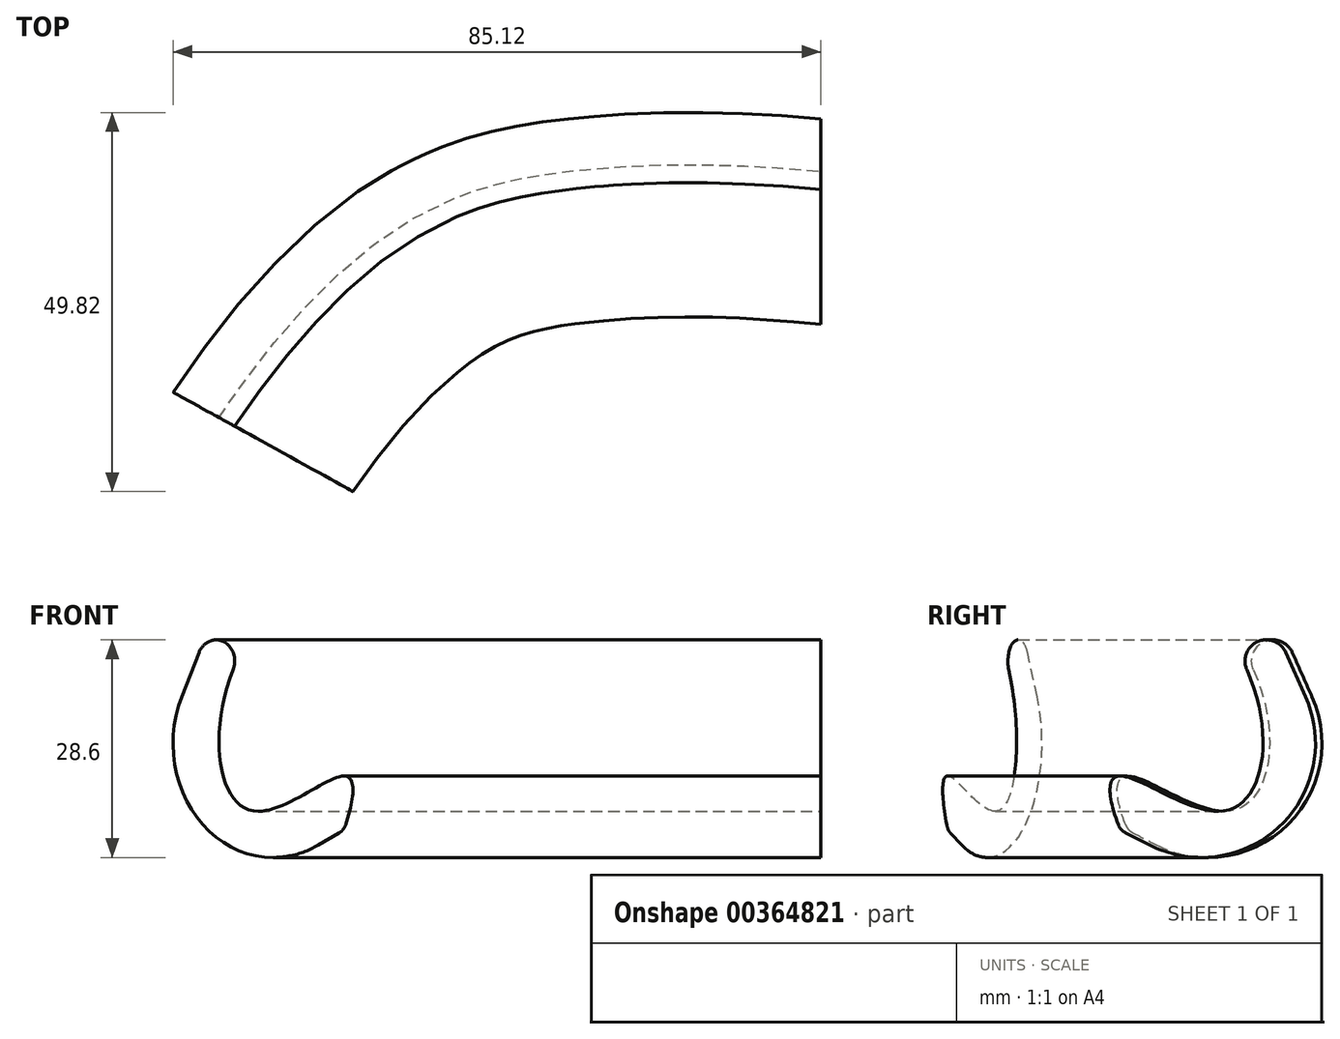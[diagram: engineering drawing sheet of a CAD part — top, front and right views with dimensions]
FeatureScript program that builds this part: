
annotation { "Feature Type Name" : "Feature", "Feature Type Description" : "" }
export const myFeature = defineFeature(function(context is Context, id is Id, definition is map)
    precondition{}
    {
        {
            var Q0;
            Q0=qCreatedBy(makeId("Right.planeOp"),FACE);
            var sketch = newSketch(context, id + "F0", { "sketchPlane" : qUnion([Q0])});
            skFitSpline(sketch, "E0", {"points": [v(-5.11, 3.54) * mm, v(-8.02, -14.99) * mm, v(-22, -10.43) * mm, v(-21.7, -17.57) * mm], "startDerivative": vector(29.4, -65.83) * mm, "endDerivative": vector(19.16, -45.51) * mm});
            skLineSegment(sketch, "E1", {"start": v(-21.02, -17.9) * mm, "end": v(-17.88, -19.5) * mm});
            skLineSegment(sketch, "E2", {"start": v(2.6, 0) * mm, "end": v(0, 5.82) * mm});
            skArc(sketch, "E3", {"start": v(0, 5.82) * mm, "mid": v(-3.7, 7.24) * mm, "end": v(-5.11, 3.54) * mm});
            skPoint(sketch, "E4.visualSharp", {"position": v(19.84, -38.61) * mm});
            skArc(sketch, "E4.filletArc", {"start": v(-17.88, -19.5) * mm, "mid": v(-0.75, -16.99) * mm, "end": v(2.6, 0) * mm});
            skArc(sketch, "E5.filletArc", {"start": v(-21.98, -16.85) * mm, "mid": v(-21.6, -17.47) * mm, "end": v(-21.02, -17.9) * mm});
            skLineSegment(sketch, "E6", {"start": v(-5.11, 3.54) * mm, "end": v(0, 5.82) * mm, "construction": true});
            skSolve(sketch);
        }
        {
            var Q0;
            Q0=qCreatedBy(makeId("Top.planeOp"),FACE);
            var sketch = newSketch(context, id + "F1", { "sketchPlane" : qUnion([Q0])});
            skFitSpline(sketch, "E7", {"points": [v(0, 0) * mm, v(-32.98, 0) * mm, v(-81.7, -33.92) * mm], "startDerivative": vector(-86.34, 7.65) * mm, "endDerivative": vector(-100.27, -148.95) * mm});
            skSolve(sketch);
        }
        {
            var Q0;
            Q0=makeQuery(id+"F0.imprint","IMPRINT",FACE,{"disambiguationData":[TD([[makeQuery(id+"F0.imprint","IMPRINT",EDGE,{"derivedFrom":sQuery(id+"F0.wireOp",EDGE,"E0")}),1.0]])]});
            var Q1;
            Q1=sQuery(id+"F1.wireOp",EDGE,"E7");
            sweep(context, id + "F2", {"profiles" : qUnion([Q0]), "path" : qUnion([Q1])});
        }
    });
